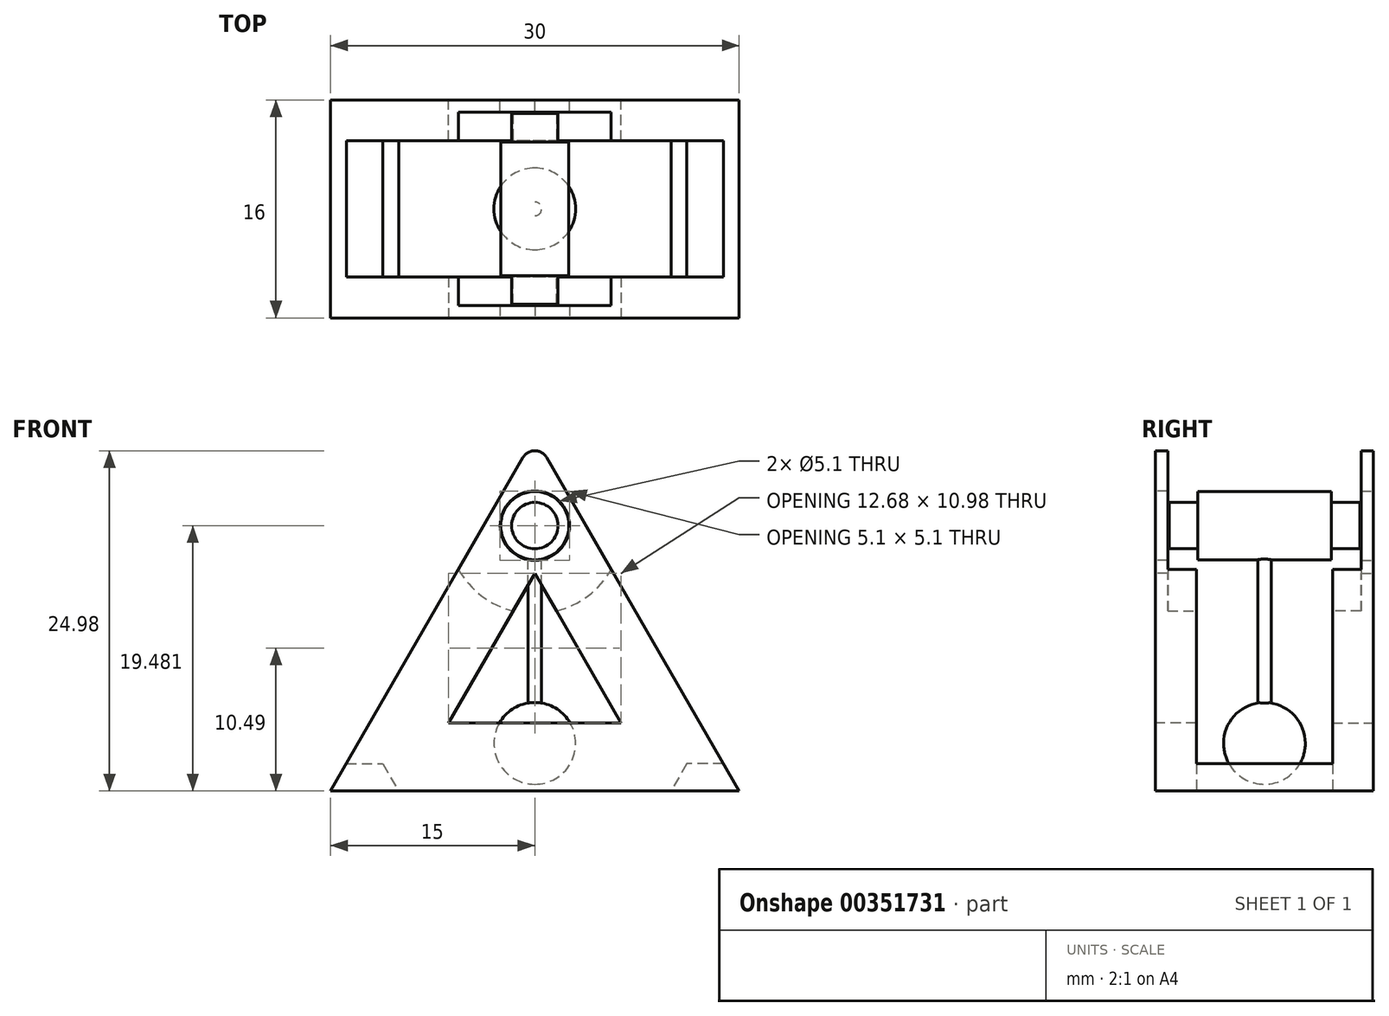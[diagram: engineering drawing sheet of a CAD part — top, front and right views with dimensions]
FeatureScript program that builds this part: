
annotation { "Feature Type Name" : "Feature", "Feature Type Description" : "" }
export const myFeature = defineFeature(function(context is Context, id is Id, definition is map)
    precondition{}
    {
        {
            var Q0;
            Q0=qCreatedBy(makeId("Front.planeOp"),FACE);
            var sketch = newSketch(context, id + "F0", { "sketchPlane" : qUnion([Q0])});
            skLineSegment(sketch, "E0", {"start": v(-15, 0) * mm, "end": v(0, 25.98) * mm});
            skLineSegment(sketch, "E1", {"start": v(0, 25.98) * mm, "end": v(15, 0) * mm});
            skLineSegment(sketch, "E2", {"start": v(15, 0) * mm, "end": v(-15, 0) * mm});
            skLineSegment(sketch, "E3", {"start": v(-6.34, 5) * mm, "end": v(0, 15.98) * mm});
            skLineSegment(sketch, "E4", {"start": v(0, 15.98) * mm, "end": v(6.34, 5) * mm});
            skLineSegment(sketch, "E5", {"start": v(6.34, 5) * mm, "end": v(-6.34, 5) * mm});
            skLineSegment(sketch, "E6", {"start": v(0, 5) * mm, "end": v(0, 0) * mm, "construction": true});
            skLineSegment(sketch, "E7", {"start": v(3.17, 10.5) * mm, "end": v(7.5, 13) * mm, "construction": true});
            skLineSegment(sketch, "E8", {"start": v(-3.17, 10.5) * mm, "end": v(-7.5, 13) * mm, "construction": true});
            skCircle(sketch, "E9", {"center": v(0, 19.48) * mm, "radius": 1.75 * mm});
            skSolve(sketch);
        }
        {
            var Q0;
            Q0 = qSketchRegion(id + "F0", true);
            extrude(context, id + "F1", {"entities" : qUnion([Q0]), "depth" : 3 * mm});
        }
        {
            var Q0;
            Q0=makeQuery(id+"F1.opExtrude","CAP_FACE",FACE,{"disambiguationData":[OSD([sQuery(id+"F0.wireOp",EDGE,"E0"),sQuery(id+"F0.wireOp",EDGE,"E1"),sQuery(id+"F0.wireOp",EDGE,"E2"),sQuery(id+"F0.wireOp",EDGE,"E3"),sQuery(id+"F0.wireOp",EDGE,"E4"),sQuery(id+"F0.wireOp",EDGE,"E5"),sQuery(id+"F0.wireOp",EDGE,"E9")])],"isStart":false});
            var sketch = newSketch(context, id + "F2", { "sketchPlane" : qUnion([Q0])});
            skLineSegment(sketch, "E10", {"start": v(-15, 0) * mm, "end": v(-13.85, 2) * mm});
            skLineSegment(sketch, "E11", {"start": v(-13.85, 2) * mm, "end": v(-11.15, 2) * mm});
            skLineSegment(sketch, "E12", {"start": v(-11.15, 2) * mm, "end": v(-10, 0) * mm});
            skLineSegment(sketch, "E13", {"start": v(-10, 0) * mm, "end": v(-15, 0) * mm});
            skLineSegment(sketch, "E14.MirrorCS", {"start": v(15, 0) * mm, "end": v(13.85, 2) * mm});
            skLineSegment(sketch, "E15.MirrorCS", {"start": v(13.85, 2) * mm, "end": v(11.15, 2) * mm});
            skLineSegment(sketch, "E16.MirrorCS", {"start": v(10, 0) * mm, "end": v(15, 0) * mm});
            skLineSegment(sketch, "E17.MirrorCS", {"start": v(11.15, 2) * mm, "end": v(10, 0) * mm});
            skSolve(sketch);
        }
        {
            var Q0;
            Q0 = qSketchRegion(id + "F2", true);
            extrude(context, id + "F3", {"entities" : qUnion([Q0]), "operationType" : NewBodyOperationType.ADD, "depth" : 5 * mm});
        }
        {
            var Q0;
            Q0=makeQuery(id+"F3.opExtrude","CAP_FACE",FACE,{"disambiguationData":[OSD([sQuery(id+"F2.wireOp",EDGE,"E10"),sQuery(id+"F2.wireOp",EDGE,"E11"),sQuery(id+"F2.wireOp",EDGE,"E12"),sQuery(id+"F2.wireOp",EDGE,"E13")])],"isStart":false});
            var sketch = newSketch(context, id + "F4", { "sketchPlane" : qUnion([Q0])});
            skCircle(sketch, "E18", {"center": v(0, 19.48) * mm, "radius": 2.5 * mm});
            skSolve(sketch);
        }
        {
            var Q0;
            Q0 = qSketchRegion(id + "F4", true);
            extrude(context, id + "F5", {"entities" : qUnion([Q0]), "oppositeDirection" : true, "depth" : 8 * mm});
        }
        {
            var Q0;
            Q0=makeQuery(id+"F1.opExtrude","CAP_FACE",FACE,{"disambiguationData":[OSD([sQuery(id+"F0.wireOp",EDGE,"E0"),sQuery(id+"F0.wireOp",EDGE,"E1"),sQuery(id+"F0.wireOp",EDGE,"E2"),sQuery(id+"F0.wireOp",EDGE,"E3"),sQuery(id+"F0.wireOp",EDGE,"E4"),sQuery(id+"F0.wireOp",EDGE,"E5"),sQuery(id+"F0.wireOp",EDGE,"E9")])],"isStart":true});
            var sketch = newSketch(context, id + "F6", { "sketchPlane" : qUnion([Q0])});
            skCircle(sketch, "E19", {"center": v(0, 19.48) * mm, "radius": 2.55 * mm});
            skSolve(sketch);
        }
        {
            var Q0;
            Q0 = qSketchRegion(id + "F6", true);
            extrude(context, id + "F7", {"entities" : qUnion([Q0]), "operationType" : NewBodyOperationType.REMOVE, "oppositeDirection" : true, "depth" : 1 * mm});
        }
        {
            var Q0;
            Q0=makeQuery(id+"F1.opExtrude","CAP_FACE",FACE,{"disambiguationData":[OSD([sQuery(id+"F0.wireOp",EDGE,"E0"),sQuery(id+"F0.wireOp",EDGE,"E1"),sQuery(id+"F0.wireOp",EDGE,"E2"),sQuery(id+"F0.wireOp",EDGE,"E3"),sQuery(id+"F0.wireOp",EDGE,"E4"),sQuery(id+"F0.wireOp",EDGE,"E5"),sQuery(id+"F0.wireOp",EDGE,"E9")])],"isStart":false});
            var sketch = newSketch(context, id + "F8", { "sketchPlane" : qUnion([Q0])});
            skCircle(sketch, "E20", {"center": v(0, 19.48) * mm, "radius": 1.7 * mm});
            skCircle(sketch, "E21", {"center": v(0, 19.48) * mm, "radius": 6.47 * mm});
            skSolve(sketch);
        }
        {
            var Q0;
            Q0 = qSketchRegion(id + "F8", true);
            extrude(context, id + "F9", {"entities" : qUnion([Q0]), "operationType" : NewBodyOperationType.REMOVE, "oppositeDirection" : true, "depth" : 2.1 * mm, "hasSecondDirection" : true, "secondDirectionOppositeDirection" : false, "secondDirectionDepth" : .1 * mm});
        }
        {
            var Q0;
            Q0=makeQuery(id+"F3.opExtrude","CAP_FACE",FACE,{"disambiguationData":[OSD([sQuery(id+"F2.wireOp",EDGE,"E10"),sQuery(id+"F2.wireOp",EDGE,"E11"),sQuery(id+"F2.wireOp",EDGE,"E12"),sQuery(id+"F2.wireOp",EDGE,"E13")])],"isStart":false});
            var sketch = newSketch(context, id + "F10", { "sketchPlane" : qUnion([Q0])});
            skCircle(sketch, "E22", {"center": v(0, 3.5) * mm, "radius": 3 * mm});
            skSolve(sketch);
        }
        {
            var Q0;
            Q0=makeQuery(id+"F10.imprint","IMPRINT",FACE,{"disambiguationData":[TD([[makeQuery(id+"F10.imprint","IMPRINT",EDGE,{"derivedFrom":sQuery(id+"F10.wireOp",EDGE,"E22")}),1.0]])]});
            extrude(context, id + "F11", {"entities" : qUnion([Q0]), "operationType" : NewBodyOperationType.ADD, "oppositeDirection" : true, "depth" : 3 * mm});
        }
        {
            var Q0;
            Q0=makeQuery(id+"F11.opExtrude","CAP_EDGE",EDGE,{"disambiguationData":[OSD([sQuery(id+"F10.wireOp",EDGE,"E22")])],"isStart":false});
            fillet(context, id + "F12", {"entities" : qUnion([Q0]), "radius" : 3 * mm, "tangentPropagation" : true, "allowEdgeOverflow" : false});
        }
        {
            var Q0;
            Q0=makeQuery(id+"F3.opExtrude","CAP_FACE",FACE,{"disambiguationData":[OSD([sQuery(id+"F2.wireOp",EDGE,"E10"),sQuery(id+"F2.wireOp",EDGE,"E11"),sQuery(id+"F2.wireOp",EDGE,"E12"),sQuery(id+"F2.wireOp",EDGE,"E13")])],"isStart":false});
            var sketch = newSketch(context, id + "F13", { "sketchPlane" : qUnion([Q0])});
            skCircle(sketch, "E23.0", {"center": v(0, 19.48) * mm, "radius": 2.5 * mm});
            skCircle(sketch, "E23.1", {"center": v(0, 3.5) * mm, "radius": 3 * mm});
            skLineSegment(sketch, "E24", {"start": v(-0.5, 17.03) * mm, "end": v(-0.5, 6.46) * mm});
            skLineSegment(sketch, "E25", {"start": v(0.5, 17.03) * mm, "end": v(0.5, 6.46) * mm});
            skSolve(sketch);
        }
        {
            var Q0;
            {var subQ0=sQuery(id+"F13.wireOp",EDGE,"E24");Q0=makeQuery(id+"F13.imprint","IMPRINT",FACE,{"disambiguationData":[TD([[makeQuery(id+"F13.imprint","IMPRINT",EDGE,{"derivedFrom":subQ0}),1.0]])]});}
            extrude(context, id + "F14", {"entities" : qUnion([Q0]), "operationType" : NewBodyOperationType.ADD, "oppositeDirection" : true, "depth" : .5 * mm});
        }
        {
            var Q0;
            Q0=makeQuery(id+"F14.opExtrude","CAP_EDGE",EDGE,{"disambiguationData":[OSD([sQuery(id+"F13.wireOp",EDGE,"E24")])],"isStart":false});
            var Q1;
            Q1=makeQuery(id+"F14.opExtrude","CAP_EDGE",EDGE,{"disambiguationData":[OSD([sQuery(id+"F13.wireOp",EDGE,"E25")])],"isStart":false});
            fillet(context, id + "F15", {"entities" : qUnion([Q0, Q1]), "radius" : .5 * mm, "tangentPropagation" : true, "allowEdgeOverflow" : false});
        }
        {
            var Q0;
            Q0=makeQuery(id+"F1.opExtrude","SWEPT_EDGE",EDGE,{"disambiguationData":[OSD([sQuery(id+"F0.wireOp",EDGE,"E0"),sQuery(id+"F0.wireOp",EDGE,"E1")])]});
            fillet(context, id + "F16", {"entities" : qUnion([Q0]), "radius" : 1 * mm, "tangentPropagation" : true, "allowEdgeOverflow" : false});
        }
        {
            var Q0;
            Q0=makeQuery(id+"F1.opExtrude","SWEPT_BODY",BODY,{"disambiguationData":[OSD([sQuery(id+"F0.wireOp",EDGE,"E0"),sQuery(id+"F0.wireOp",EDGE,"E1"),sQuery(id+"F0.wireOp",EDGE,"E2"),sQuery(id+"F0.wireOp",EDGE,"E3"),sQuery(id+"F0.wireOp",EDGE,"E4"),sQuery(id+"F0.wireOp",EDGE,"E5"),sQuery(id+"F0.wireOp",EDGE,"E9")])]});
            var Q1;
            Q1=makeQuery(id+"F5.opExtrude","SWEPT_BODY",BODY,{"disambiguationData":[OSD([sQuery(id+"F4.wireOp",EDGE,"E18")])]});
            var Q2;
            Q2=makeQuery(id+"F11.opExtrude","SWEPT_BODY",BODY,{"disambiguationData":[OSD([sQuery(id+"F10.wireOp",EDGE,"E22")])]});
            var Q3;
            Q3=makeQuery(id+"F3.opExtrude","CAP_FACE",FACE,{"disambiguationData":[OSD([sQuery(id+"F2.wireOp",EDGE,"E10"),sQuery(id+"F2.wireOp",EDGE,"E11"),sQuery(id+"F2.wireOp",EDGE,"E12"),sQuery(id+"F2.wireOp",EDGE,"E13")])],"isStart":false});
            mirror(context, id + "F17", {"operationType" : NewBodyOperationType.ADD, "entities" : qUnion([Q0, Q1, Q2]), "mirrorPlane" : qUnion([Q3])});
        }
    });
